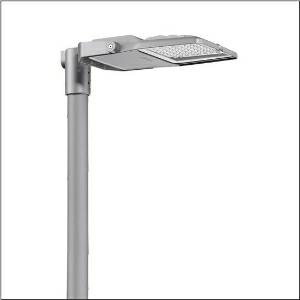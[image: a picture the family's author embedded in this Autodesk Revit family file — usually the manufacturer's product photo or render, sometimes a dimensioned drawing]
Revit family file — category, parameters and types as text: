
# Revit family: floodlight_fl_21_iq_mini___pl52_5xa7772c2d3a_4b1a
name_source: partatom
category: Lighting Fixtures
units: mm (PartAtom-declared; Revit-internal decimal feet)

## family parameters
Cut with Voids When Loaded = No
Host = Face
Light Source = No
Part Type = Normal
Room Calculation Point = No
Round Connector Dimension = Use Diameter
Shared = No

## types (1)
- --- (1 x LED, 12210 lm, 87.2 W, 3000K)
    Apparent Load = 87 VA
    CIE Flux Codes = 26 60 98 100 100
    Color Rendering = 70
    Color Temperature = 3000K
    Default Elevation = 1800 mm
    Description = Floodlight FL 21 iQ mini, floodlight, primary light control with lens, of PMMA, primary optical cover: protective disc, of toughened safety glass, transparent, light distribution: PL52, light emission: direct distribution, installation type: surface-mounted, LED, High Power LED, rated luminous flux: 12.210lm, luminous efficacy: 140lm/W, light colour: 730, colour temperature: 3000K, control gear: iQ Street-Remote/DALI, control: Auto-Match, Temp-Guard, Night-Set, Smart-Wire, Desk-Remote (wireless, voltage-free reading and setting of iQ features in the workshop via application-optimized NFC function/RFID function), optimised constant luminous flux control (CLO 2.0), Light-Fading, Lumen-Switch, with terminal, 6-pole, mains connection: 220..240V, AC, 50/60Hz, start of lifetime: 87W, end of service life: 92W, reduction: 40W, luminaire housing, of diecast aluminium, powder-coated, Siteco® metallic grey (DB 702S), corrosivity category C5 mid according to DIN EN ISO 12944, suitable for swimming pools, chlorine-resistant, sealing non-destructively replaceable, please order mast flange separately, mast bracket, of steel, galvanised, powder-coated, protection rating (complete): IP66, insulation class (complete): insulation class II (safety insulation), certification: CE, ENEC, VDE, protection symbol: D, impact resistance: IK08, permissible operating ambient temperature: -40..+40°C, permissible operating ambient temperature for outdoor applications: -40..+50°C, standard: DIN EN 12944, LABS conformity tested according to VDMA 24364:2018-05, packaging unit: 1 piece

Light Distribution: PL52
    Height = 70 mm
    Lamp = 1 x LED
    Lamp Light Flux = 12210 lm
    Lamp Power = 87.2 W
    Lamp count = 1
    Length = 485 mm
    Luminous efficacy = 140 lm/W
    Manufacturer = Siteco
    ModVariant = No
    Model = 5XA7772C2D3A
    Number of Poles = 1
    OnlyDefault = Yes
    Power Factor = 1
    Product Name = Floodlight FL 21 iQ mini | PL52
    Product group = floodlight | pylon annexe
    ProductGroupID = 6200
    Protection Class = Protection class II
    Protection Degree = IP 66
    RLX_Detail_Level = 1
    RLX_Emergency_Light_Flux = 0 lm
    RLX_Emergency_Type = 0
    RLX_Emergency_Type_DB = No
    RlxData = <blob elided: 101525 chars, md5=047641fc>
    Socket = socket
    Standby Power = 0 W
    System Light Flux = 12210 lm
    System Power = 87 W
    Type Comments = factory setting: luminous flux: 100 % | dim-lin: 254 | 456 mA
    Type Image = l_1007125.jpg
    URL = http://relux.com
    VarID = @adj_164304
    Voltage = 0 V
    Weight = 0.00 kg
    Width = 337 mm

## geometry (parser evidence)
native form markers: Blend x4, Sweep x13
no freeform markers — native parametric forms only
